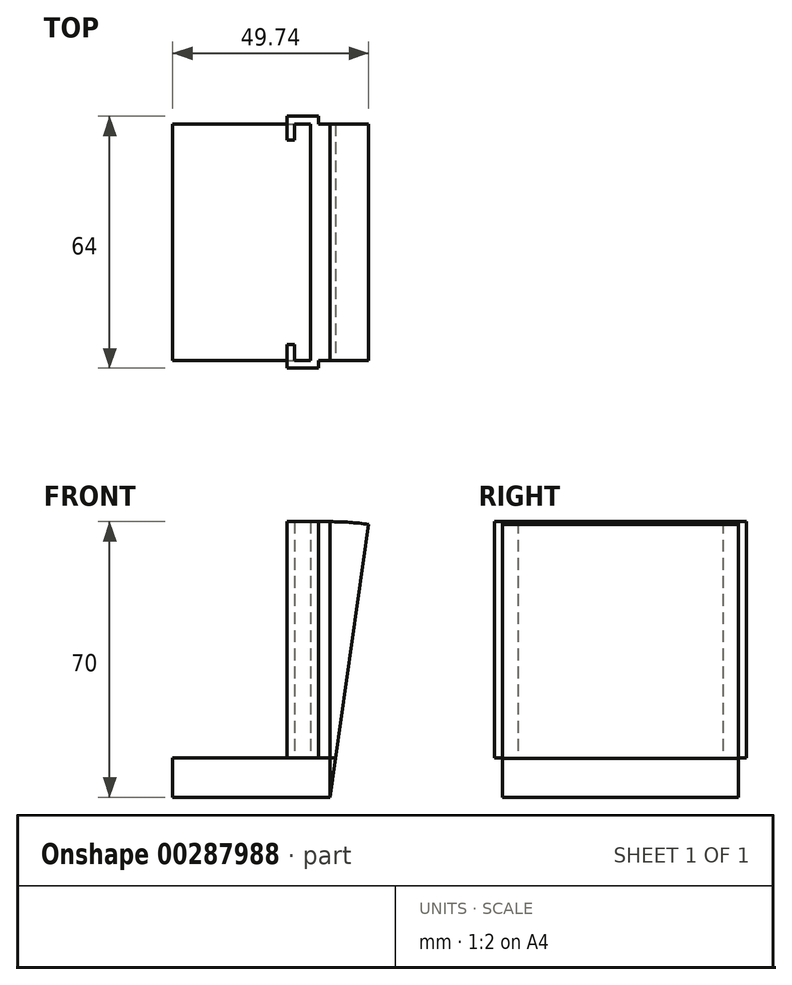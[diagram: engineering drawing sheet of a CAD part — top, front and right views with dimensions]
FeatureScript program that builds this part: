
annotation { "Feature Type Name" : "Feature", "Feature Type Description" : "" }
export const myFeature = defineFeature(function(context is Context, id is Id, definition is map)
    precondition{}
    {
        {
            var Q0;
            Q0=qCreatedBy(makeId("Top.planeOp"),FACE);
            var sketch = newSketch(context, id + "F0", { "sketchPlane" : qUnion([Q0])});
            skLineSegment(sketch, "E0.left", {"start": v(-5, 30) * mm, "end": v(-5, -30) * mm});
            skPoint(sketch, "E0.middle", {"position": v(0, 0) * mm});
            skLineSegment(sketch, "E1.MirrorCS", {"start": v(-5, -30) * mm, "end": v(-5, 30) * mm});
            skLineSegment(sketch, "E2.left", {"start": v(-5, 23.5) * mm, "end": v(-5, -23.5) * mm});
            skPoint(sketch, "E3", {"position": v(-3, 30) * mm});
            skLineSegment(sketch, "E4.bottom", {"start": v(-3, 30) * mm, "end": v(-11, 30) * mm});
            skLineSegment(sketch, "E4.top", {"start": v(-3, 32) * mm, "end": v(-11, 32) * mm});
            skLineSegment(sketch, "E4.left", {"start": v(-3, 30) * mm, "end": v(-3, 32) * mm});
            skLineSegment(sketch, "E4.right", {"start": v(-11, 30) * mm, "end": v(-11, 32) * mm});
            skLineSegment(sketch, "E5.bottom", {"start": v(-11, 32) * mm, "end": v(-9, 32) * mm});
            skLineSegment(sketch, "E5.top", {"start": v(-11, 26) * mm, "end": v(-9, 26) * mm});
            skLineSegment(sketch, "E5.left", {"start": v(-11, 32) * mm, "end": v(-11, 26) * mm});
            skLineSegment(sketch, "E5.right", {"start": v(-9, 32) * mm, "end": v(-9, 26) * mm});
            skLineSegment(sketch, "E6.MirrorCS", {"start": v(-11, -32) * mm, "end": v(-9, -32) * mm});
            skLineSegment(sketch, "E7.MirrorCS", {"start": v(-3, -30) * mm, "end": v(-3, -32) * mm});
            skLineSegment(sketch, "E8.MirrorCS", {"start": v(-11, -30) * mm, "end": v(-11, -32) * mm});
            skLineSegment(sketch, "E9.MirrorCS", {"start": v(-3, -30) * mm, "end": v(-11, -30) * mm});
            skPoint(sketch, "E10.MirrorP", {"position": v(-3, -30) * mm});
            skLineSegment(sketch, "E11.MirrorCS", {"start": v(-3, -32) * mm, "end": v(-11, -32) * mm});
            skLineSegment(sketch, "E12.MirrorCS", {"start": v(-11, -26) * mm, "end": v(-9, -26) * mm});
            skLineSegment(sketch, "E13.MirrorCS", {"start": v(-9, -32) * mm, "end": v(-9, -26) * mm});
            skLineSegment(sketch, "E14.MirrorCS", {"start": v(-11, -32) * mm, "end": v(-11, -26) * mm});
            skLineSegment(sketch, "E15.left", {"start": v(0, 30) * mm, "end": v(0, -30) * mm});
            skLineSegment(sketch, "E16.bottom", {"start": v(-5, 30) * mm, "end": v(0, 30) * mm});
            skLineSegment(sketch, "E16.top", {"start": v(-5, -30) * mm, "end": v(0, -30) * mm});
            skSolve(sketch);
        }
        {
            var Q0;
            Q0=qSketchRegion(id+"F0",true);
            extrude(context, id + "F1", {"entities" : qUnion([Q0]), "depth" : 60 * mm});
        }
        {
            var Q0;
            Q0=qCreatedBy(makeId("Right.planeOp"),FACE);
            var sketch = newSketch(context, id + "F2", { "sketchPlane" : qUnion([Q0])});
            skLineSegment(sketch, "E17.bottom", {"start": v(-30, 0) * mm, "end": v(30, 0) * mm});
            skLineSegment(sketch, "E17.top", {"start": v(-30, -10) * mm, "end": v(30, -10) * mm});
            skLineSegment(sketch, "E17.left", {"start": v(-30, 0) * mm, "end": v(-30, -10) * mm});
            skLineSegment(sketch, "E17.right", {"start": v(30, 0) * mm, "end": v(30, -10) * mm});
            skSolve(sketch);
        }
        {
            var Q0;
            Q0=makeQuery(id+"F2.imprint","IMPRINT",FACE,{"disambiguationData":[TD([[makeQuery(id+"F2.imprint","IMPRINT",EDGE,{"derivedFrom":sQuery(id+"F2.wireOp",EDGE,"E17.bottom")}),-1.0]])]});
            extrude(context, id + "F3", {"entities" : qUnion([Q0]), "oppositeDirection" : true, "depth" : 40 * mm});
        }
        {
            var Q0;
            Q0=makeQuery(id+"F2.imprint","IMPRINT",FACE,{"disambiguationData":[TD([[makeQuery(id+"F2.imprint","IMPRINT",EDGE,{"derivedFrom":sQuery(id+"F2.wireOp",EDGE,"E17.bottom")}),-1.0]])]});
            var Q1;
            Q1=makeQuery(id+"F1.opExtrude","SWEPT_FACE",FACE,{"disambiguationData":[OSD([sQuery(id+"F0.wireOp",EDGE,"E15.left")])]});
            var Q2;
            Q2=sQuery(id+"F2.wireOp",EDGE,"E17.top");
            revolve(context, id + "F4", {"entities" : qUnion([Q0, Q1]), "axis" : qUnion([Q2]), "revolveType" : RevolveType.ONE_DIRECTION, "angle" : 8 * degree});
        }
    });
